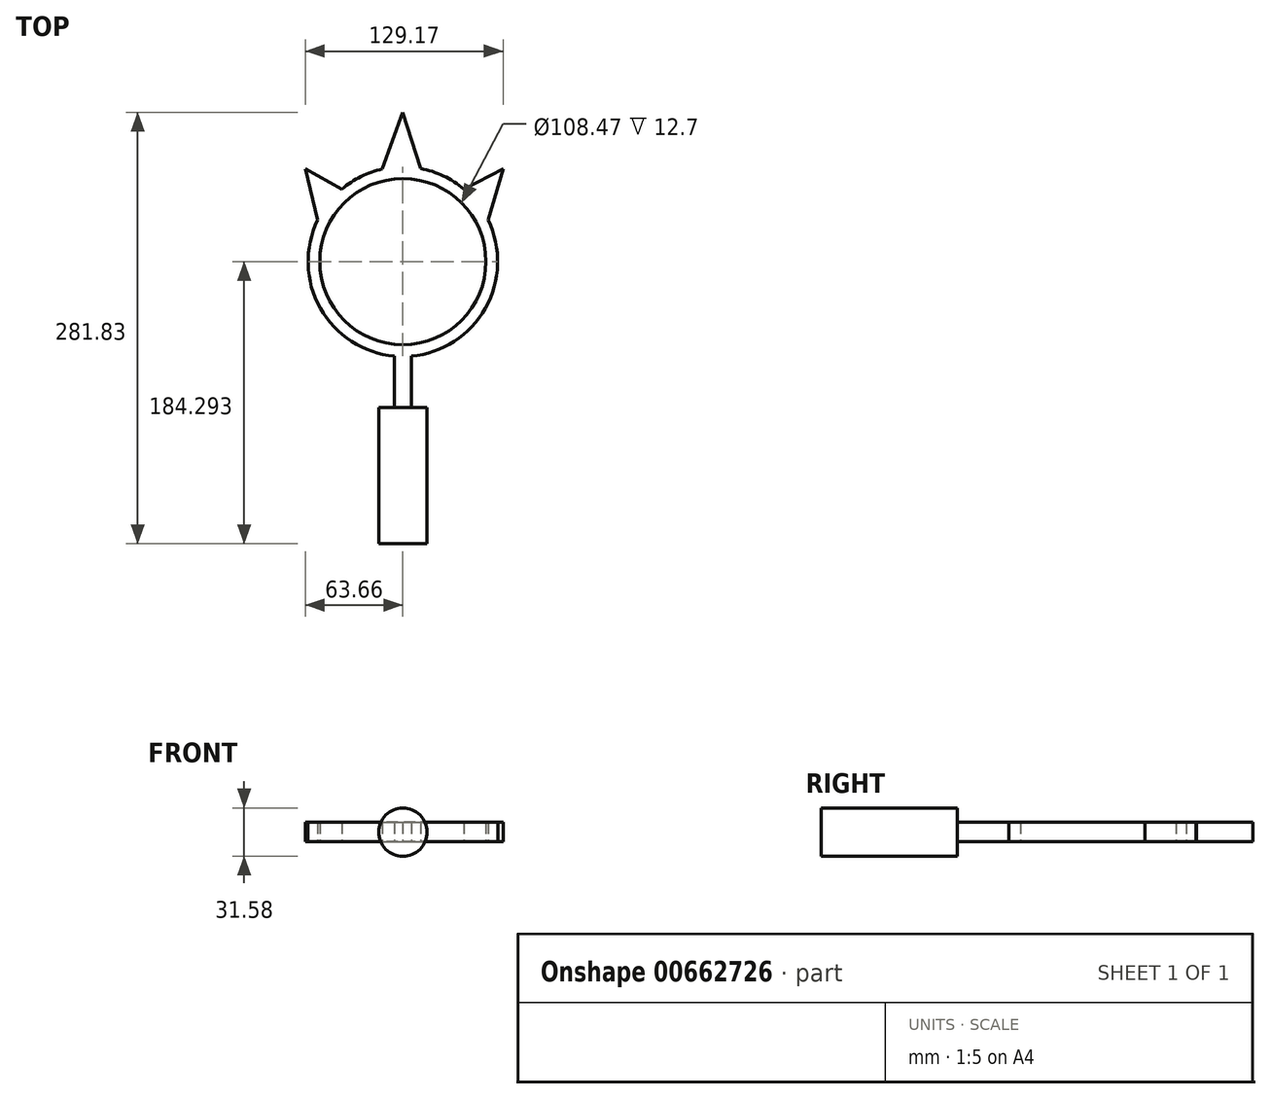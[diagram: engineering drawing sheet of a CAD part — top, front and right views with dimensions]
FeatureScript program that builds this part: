
annotation { "Feature Type Name" : "Feature", "Feature Type Description" : "" }
export const myFeature = defineFeature(function(context is Context, id is Id, definition is map)
    precondition{}
    {
        {
            var Q0;
            Q0=qCreatedBy(makeId("Top.planeOp"),FACE);
            var sketch = newSketch(context, id + "F0", { "sketchPlane" : qUnion([Q0])});
            skCircle(sketch, "E0", {"center": v(0, 40.6) * mm, "radius": 54.24 * mm});
            skCircle(sketch, "E1", {"center": v(0, 40.6) * mm, "radius": 61.92 * mm});
            skLineSegment(sketch, "E2.bottom", {"start": v(-5.57, -21.07) * mm, "end": v(5.68, -21.07) * mm});
            skLineSegment(sketch, "E2.top", {"start": v(-5.57, -58.26) * mm, "end": v(5.68, -58.26) * mm});
            skLineSegment(sketch, "E2.left", {"start": v(-5.57, -21.07) * mm, "end": v(-5.57, -58.26) * mm});
            skLineSegment(sketch, "E2.right", {"start": v(5.68, -21.07) * mm, "end": v(5.68, -58.26) * mm});
            skLineSegment(sketch, "E3.bottom", {"start": v(-13.34, -58.26) * mm, "end": v(13.13, -58.26) * mm});
            skLineSegment(sketch, "E3.top", {"start": v(-13.34, -143.07) * mm, "end": v(13.13, -143.07) * mm});
            skLineSegment(sketch, "E3.left", {"start": v(-13.34, -58.26) * mm, "end": v(-13.34, -143.07) * mm});
            skLineSegment(sketch, "E3.right", {"start": v(13.13, -58.26) * mm, "end": v(13.13, -143.07) * mm});
            skLineSegment(sketch, "E4", {"start": v(-13.37, 101.06) * mm, "end": v(0, 138.14) * mm});
            skLineSegment(sketch, "E5", {"start": v(0, 138.14) * mm, "end": v(11.57, 101.44) * mm});
            skLineSegment(sketch, "E6", {"start": v(39.8, 88.04) * mm, "end": v(65.5, 101.06) * mm});
            skLineSegment(sketch, "E7", {"start": v(65.5, 101.06) * mm, "end": v(55.65, 67.75) * mm});
            skLineSegment(sketch, "E8", {"start": v(-39.8, 88.04) * mm, "end": v(-63.66, 101.06) * mm});
            skLineSegment(sketch, "E9", {"start": v(-63.66, 101.06) * mm, "end": v(-55.65, 67.75) * mm});
            skSolve(sketch);
        }
        {
            var Q0;
            Q0=makeQuery(id+"F0.imprint","IMPRINT",FACE,{"disambiguationData":[TD([[makeQuery(id+"F0.imprint","IMPRINT",EDGE,{"derivedFrom":sQuery(id+"F0.wireOp",EDGE,"E0")}),-1.0]])]});
            var Q1;
            {var subQ0=sQuery(id+"F0.wireOp",EDGE,"E4");Q1=makeQuery(id+"F0.imprint","IMPRINT",FACE,{"disambiguationData":[TD([[makeQuery(id+"F0.imprint","IMPRINT",EDGE,{"derivedFrom":subQ0}),-1.0]])]});}
            var Q2;
            Q2 = qSketchRegion(id + "F0", true);
            var Q3;
            {var subQ0=sQuery(id+"F0.wireOp",EDGE,"E8");Q3=makeQuery(id+"F0.imprint","IMPRINT",FACE,{"disambiguationData":[TD([[makeQuery(id+"F0.imprint","IMPRINT",EDGE,{"derivedFrom":subQ0}),1.0]])]});}
            var Q4;
            {var subQ0=sQuery(id+"F0.wireOp",EDGE,"E6");Q4=makeQuery(id+"F0.imprint","IMPRINT",FACE,{"disambiguationData":[TD([[makeQuery(id+"F0.imprint","IMPRINT",EDGE,{"derivedFrom":subQ0}),-1.0]])]});}
            extrude(context, id + "F1", {"entities" : qUnion([Q0, Q1, Q2, Q3, Q4]), "depth" : 12.7 * mm, "offsetDistance" : 25.4 * mm});
        }
        {
            var Q0;
            Q0=qCreatedBy(makeId("Front.planeOp"),FACE);
            var sketch = newSketch(context, id + "F2", { "sketchPlane" : qUnion([Q0])});
            skCircle(sketch, "E10", {"center": v(0, 6.25) * mm, "radius": 15.8 * mm});
            skSolve(sketch);
        }
        {
            var Q0;
            Q0=makeQuery(id+"F2.imprint","IMPRINT",FACE,{"disambiguationData":[TD([[makeQuery(id+"F2.imprint","IMPRINT",EDGE,{"derivedFrom":sQuery(id+"F2.wireOp",EDGE,"E10")}),1.0]])]});
            extrude(context, id + "F3", {"entities" : qUnion([Q0]), "operationType" : NewBodyOperationType.ADD, "depth" : 143.7 * mm, "offsetDistance" : 25.4 * mm, "hasSecondDirection" : true, "secondDirectionOppositeDirection" : false, "secondDirectionDepth" : 54.7 * mm});
        }
    });
